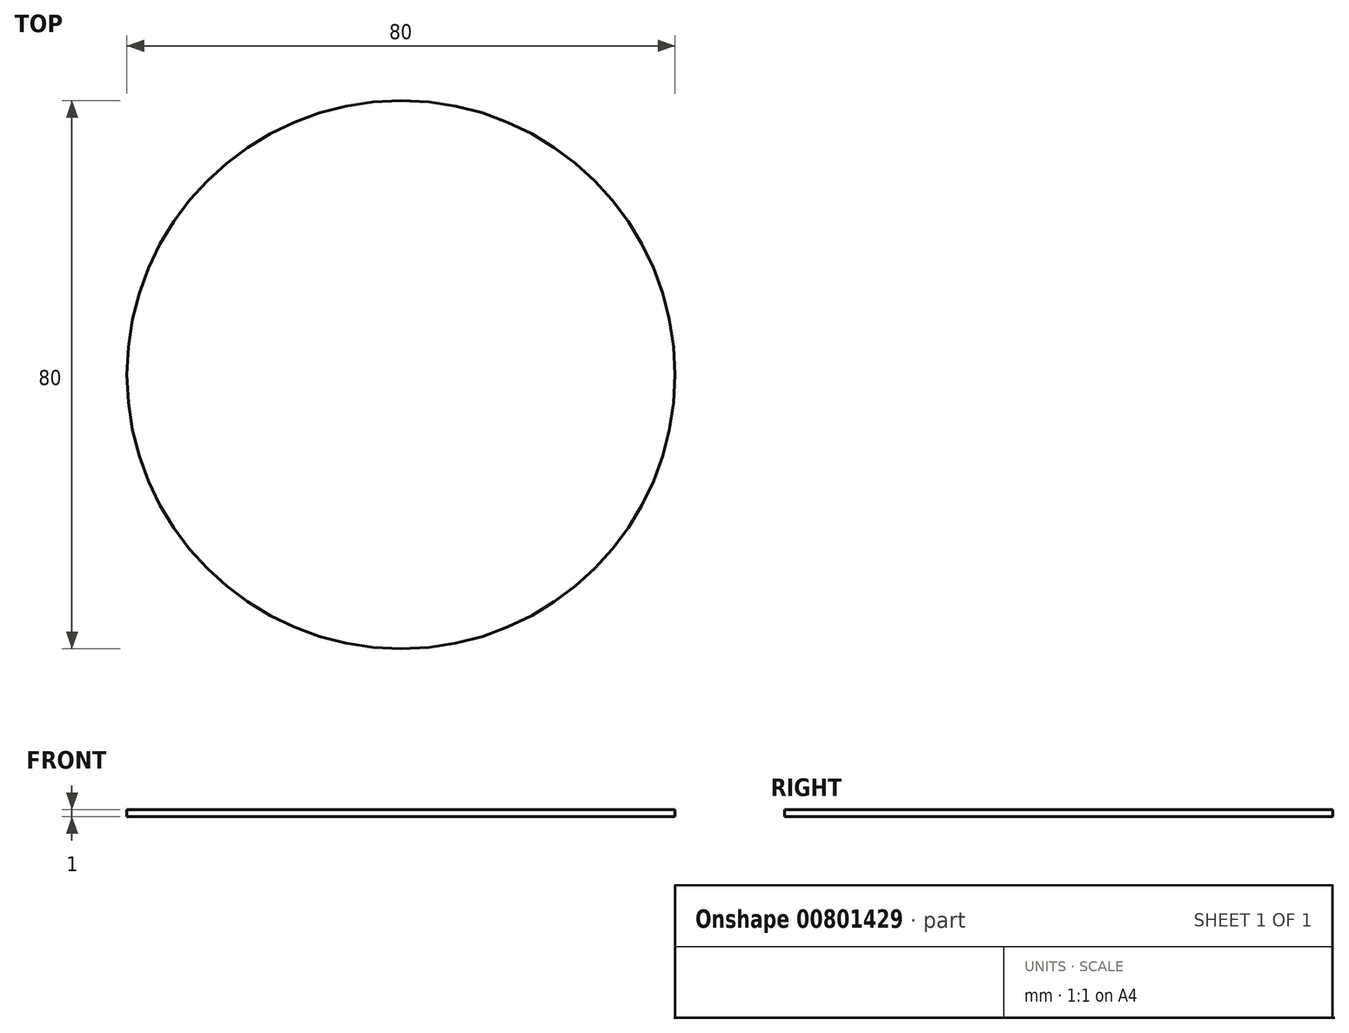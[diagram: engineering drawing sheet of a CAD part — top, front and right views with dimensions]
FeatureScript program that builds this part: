
annotation { "Feature Type Name" : "Feature", "Feature Type Description" : "" }
export const myFeature = defineFeature(function(context is Context, id is Id, definition is map)
    precondition{}
    {
        {
            var Q0;
            Q0=qCreatedBy(makeId("Top.planeOp"),FACE);
            var sketch = newSketch(context, id + "F0", { "sketchPlane" : qUnion([Q0])});
            skCircle(sketch, "E0", {"center": v(0, 0) * mm, "radius": 40 * mm});
            skSolve(sketch);
        }
        {
            var Q0;
            Q0=makeQuery(id+"F0.imprint","IMPRINT",FACE,{"disambiguationData":[TD([[makeQuery(id+"F0.imprint","IMPRINT",EDGE,{"derivedFrom":sQuery(id+"F0.wireOp",EDGE,"E0")}),1.0]])]});
            extrude(context, id + "F1", {"entities" : qUnion([Q0]), "depth" : 1 * mm, "offsetDistance" : 25 * mm});
        }
    });
